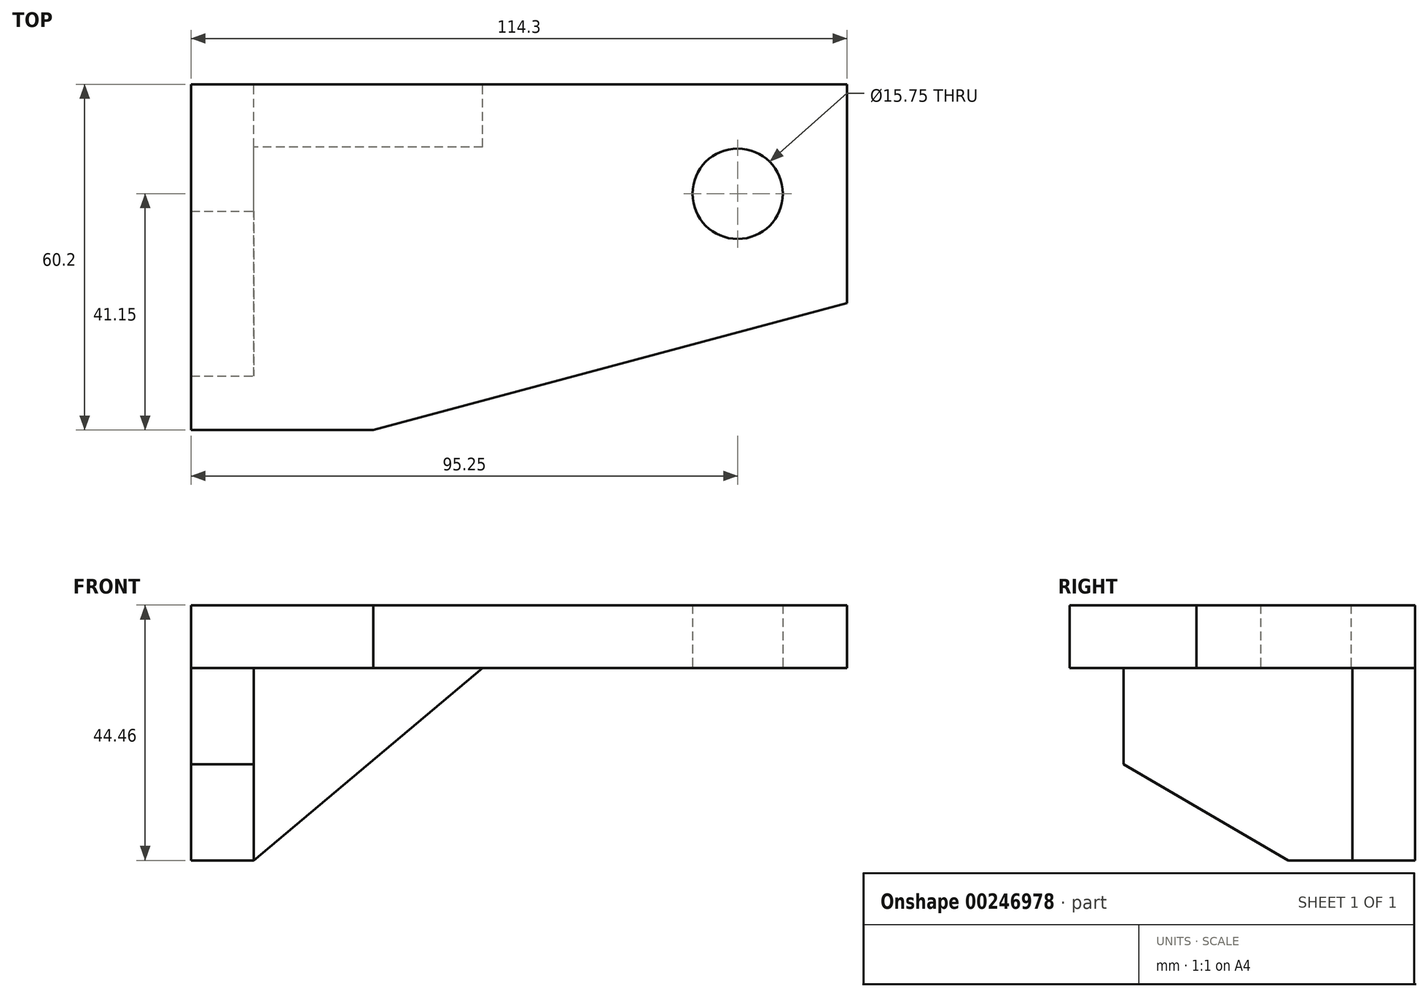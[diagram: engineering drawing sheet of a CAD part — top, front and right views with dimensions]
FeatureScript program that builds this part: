
annotation { "Feature Type Name" : "Feature", "Feature Type Description" : "" }
export const myFeature = defineFeature(function(context is Context, id is Id, definition is map)
    precondition{}
    {
        {
            var Q0;
            Q0=qCreatedBy(makeId("Front.planeOp"),FACE);
            var sketch = newSketch(context, id + "F0", { "sketchPlane" : qUnion([Q0])});
            skLineSegment(sketch, "E0.bottom", {"start": v(57.15, 22.23) * mm, "end": v(-57.15, 22.23) * mm});
            skLineSegment(sketch, "E0.top", {"start": v(-46.23, -22.23) * mm, "end": v(-57.15, -22.23) * mm});
            skLineSegment(sketch, "E0.left", {"start": v(57.15, 22.23) * mm, "end": v(57.15, 11.3) * mm});
            skLineSegment(sketch, "E0.right", {"start": v(-57.15, 22.23) * mm, "end": v(-57.15, -22.23) * mm});
            skPoint(sketch, "E0.middle", {"position": v(0, 0) * mm});
            skLineSegment(sketch, "E1.top", {"start": v(57.15, 11.3) * mm, "end": v(-46.23, 11.3) * mm});
            skLineSegment(sketch, "E1.right", {"start": v(-57.15, 22.23) * mm, "end": v(-57.15, 11.3) * mm});
            skLineSegment(sketch, "E2.bottom", {"start": v(-57.15, -22.23) * mm, "end": v(-46.23, -22.23) * mm});
            skLineSegment(sketch, "E2.left", {"start": v(-57.15, -22.23) * mm, "end": v(-57.15, 11.3) * mm});
            skLineSegment(sketch, "E2.right", {"start": v(-46.23, -22.23) * mm, "end": v(-46.23, 11.3) * mm});
            skLineSegment(sketch, "E3.top", {"start": v(-46.23, 11.3) * mm, "end": v(-6.35, 11.3) * mm});
            skPoint(sketch, "E4.orphan", {"position": v(57.15, -22.23) * mm});
            skLineSegment(sketch, "E5", {"start": v(-6.35, 11.3) * mm, "end": v(-46.23, -22.23) * mm});
            skLineSegment(sketch, "E6", {"start": v(-46.23, 11.3) * mm, "end": v(-57.15, 11.3) * mm});
            skSolve(sketch);
        }
        {
            var Q0;
            Q0=makeQuery(id+"F0.imprint","IMPRINT",FACE,{"disambiguationData":[TD([[makeQuery(id+"F0.imprint","IMPRINT",EDGE,{"derivedFrom":sQuery(id+"F0.wireOp",EDGE,"E2.right")}),-1.0]])]});
            extrude(context, id + "F1", {"entities" : qUnion([Q0]), "depth" : 10.92 * mm});
        }
        {
            var Q0;
            Q0=makeQuery(id+"F0.imprint","IMPRINT",FACE,{"disambiguationData":[TD([[makeQuery(id+"F0.imprint","IMPRINT",EDGE,{"derivedFrom":sQuery(id+"F0.wireOp",EDGE,"E2.right")}),1.0]])]});
            extrude(context, id + "F2", {"entities" : qUnion([Q0]), "operationType" : NewBodyOperationType.ADD, "depth" : 50.8 * mm});
        }
        {
            var Q0;
            Q0=makeQuery(id+"F0.imprint","IMPRINT",FACE,{"disambiguationData":[TD([[makeQuery(id+"F0.imprint","IMPRINT",EDGE,{"derivedFrom":sQuery(id+"F0.wireOp",EDGE,"E0.bottom")}),1.0]])]});
            extrude(context, id + "F3", {"entities" : qUnion([Q0]), "operationType" : NewBodyOperationType.ADD, "depth" : 60.2 * mm});
        }
        {
            var Q0;
            Q0=makeQuery(id+"F3.opExtrude","SWEPT_FACE",FACE,{"disambiguationData":[OSD([sQuery(id+"F0.wireOp",EDGE,"E1.top"),sQuery(id+"F0.wireOp",EDGE,"E3.top"),sQuery(id+"F0.wireOp",EDGE,"E6")])]});
            var sketch = newSketch(context, id + "F4", { "sketchPlane" : qUnion([Q0])});
            skLineSegment(sketch, "E7", {"start": v(-57.15, 60.2) * mm, "end": v(-25.4, 60.2) * mm});
            skLineSegment(sketch, "E8", {"start": v(-25.4, 60.2) * mm, "end": v(57.15, 38.08) * mm});
            skLineSegment(sketch, "E9", {"start": v(57.15, 0) * mm, "end": v(38.1, 0) * mm});
            skLineSegment(sketch, "E10", {"start": v(38.1, 0) * mm, "end": v(38.1, 19.05) * mm});
            skCircle(sketch, "E11", {"center": v(38.1, 19.05) * mm, "radius": 7.87 * mm});
            skSolve(sketch);
        }
        {
            var Q0;
            Q0 = qSketchRegion(id + "F4", true);
            var Q1;
            {var subQ0=sQuery(id+"F4.wireOp",EDGE,"E8");Q1=makeQuery(id+"F4.imprint","IMPRINT",FACE,{"disambiguationData":[TD([[makeQuery(id+"F4.imprint","IMPRINT",EDGE,{"derivedFrom":subQ0}),1.0]])]});}
            extrude(context, id + "F5", {"entities" : qUnion([Q0, Q1]), "operationType" : NewBodyOperationType.REMOVE, "endBound" : BoundingType.THROUGH_ALL, "oppositeDirection" : true, "depth" : 25.4 * mm});
        }
        {
            var Q0;
            Q0=makeQuery(id+"F2.opExtrude","SWEPT_FACE",FACE,{"disambiguationData":[OSD([sQuery(id+"F0.wireOp",EDGE,"E2.right")])]});
            var sketch = newSketch(context, id + "F6", { "sketchPlane" : qUnion([Q0])});
            skLineSegment(sketch, "E12", {"start": v(-50.8, -22.23) * mm, "end": v(-22.1, -22.23) * mm});
            skLineSegment(sketch, "E13", {"start": v(-22.1, -22.23) * mm, "end": v(-50.8, -5.46) * mm});
            skSolve(sketch);
        }
        {
            var Q0;
            {var subQ0=sQuery(id+"F6.wireOp",EDGE,"E12");Q0=makeQuery(id+"F6.imprint","IMPRINT",FACE,{"disambiguationData":[TD([[makeQuery(id+"F6.imprint","IMPRINT",EDGE,{"derivedFrom":subQ0}),1.0]])]});}
            extrude(context, id + "F7", {"entities" : qUnion([Q0]), "operationType" : NewBodyOperationType.REMOVE, "endBound" : BoundingType.THROUGH_ALL, "oppositeDirection" : true, "depth" : 25.4 * mm});
        }
    });
